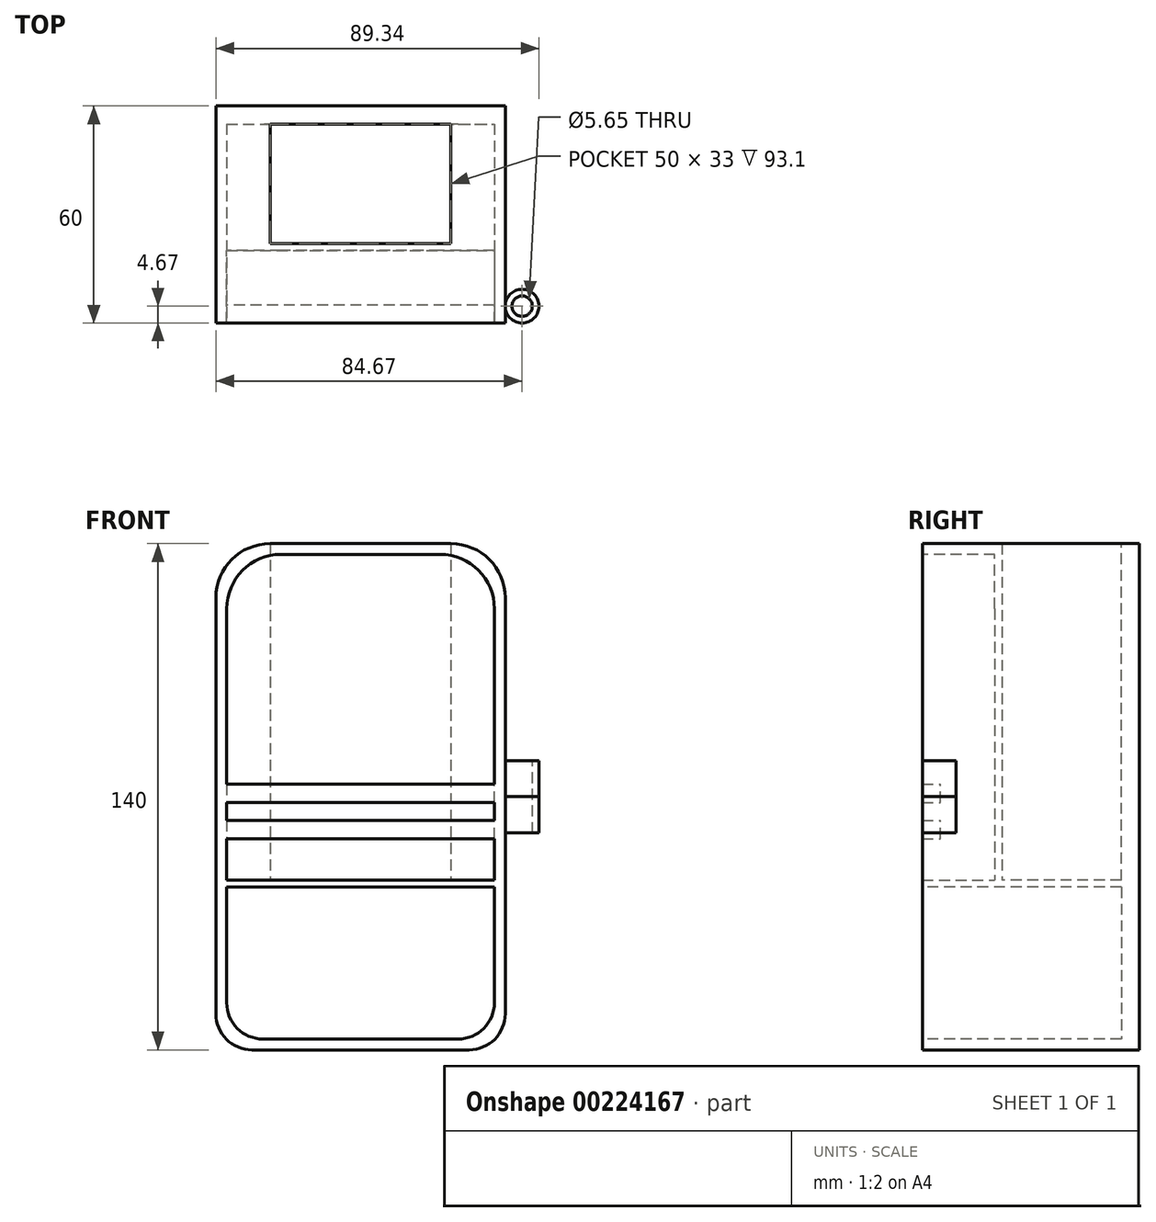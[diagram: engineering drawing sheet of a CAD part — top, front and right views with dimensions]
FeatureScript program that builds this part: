
annotation { "Feature Type Name" : "Feature", "Feature Type Description" : "" }
export const myFeature = defineFeature(function(context is Context, id is Id, definition is map)
    precondition{}
    {
        {
            var Q0;
            Q0=qCreatedBy(makeId("Front.planeOp"),FACE);
            var sketch = newSketch(context, id + "F0", { "sketchPlane" : qUnion([Q0])});
            skLineSegment(sketch, "E0.bottom", {"start": v(40, 70) * mm, "end": v(-40, 70) * mm});
            skLineSegment(sketch, "E0.top", {"start": v(40, -70) * mm, "end": v(-40, -70) * mm});
            skLineSegment(sketch, "E0.left", {"start": v(40, 70) * mm, "end": v(40, -70) * mm});
            skLineSegment(sketch, "E0.right", {"start": v(-40, 70) * mm, "end": v(-40, -70) * mm});
            skPoint(sketch, "E0.middle", {"position": v(0, 0) * mm});
            skSolve(sketch);
        }
        {
            var Q0;
            Q0=makeQuery(id+"F0.imprint","IMPRINT",FACE,{"disambiguationData":[TD([[makeQuery(id+"F0.imprint","IMPRINT",EDGE,{"derivedFrom":sQuery(id+"F0.wireOp",EDGE,"E0.bottom")}),1.0]])]});
            extrude(context, id + "F1", {"entities" : qUnion([Q0]), "oppositeDirection" : true, "depth" : 60 * mm});
        }
        {
            var Q0;
            Q0=makeQuery(id+"F1.opExtrude","SWEPT_EDGE",EDGE,{"disambiguationData":[OSD([sQuery(id+"F0.wireOp",EDGE,"E0.bottom"),sQuery(id+"F0.wireOp",EDGE,"E0.right")])]});
            fillet(context, id + "F2", {"entities" : qUnion([Q0]), "radius" : 15 * mm, "tangentPropagation" : true, "allowEdgeOverflow" : false});
        }
        {
            var Q0;
            Q0=makeQuery(id+"F1.opExtrude","SWEPT_EDGE",EDGE,{"disambiguationData":[OSD([sQuery(id+"F0.wireOp",EDGE,"E0.bottom"),sQuery(id+"F0.wireOp",EDGE,"E0.left")])]});
            fillet(context, id + "F3", {"entities" : qUnion([Q0]), "radius" : 15 * mm, "tangentPropagation" : true, "allowEdgeOverflow" : false});
        }
        {
            var Q0;
            Q0=makeQuery(id+"F1.opExtrude","SWEPT_EDGE",EDGE,{"disambiguationData":[OSD([sQuery(id+"F0.wireOp",EDGE,"E0.top"),sQuery(id+"F0.wireOp",EDGE,"E0.right")])]});
            var Q1;
            Q1=makeQuery(id+"F1.opExtrude","SWEPT_EDGE",EDGE,{"disambiguationData":[OSD([sQuery(id+"F0.wireOp",EDGE,"E0.top"),sQuery(id+"F0.wireOp",EDGE,"E0.left")])]});
            fillet(context, id + "F4", {"entities" : qUnion([Q0, Q1]), "radius" : 10 * mm, "tangentPropagation" : true, "allowEdgeOverflow" : false});
        }
        {
            var Q0;
            Q0=makeQuery(id+"F1.opExtrude","CAP_FACE",FACE,{"disambiguationData":[OSD([sQuery(id+"F0.wireOp",EDGE,"E0.bottom"),sQuery(id+"F0.wireOp",EDGE,"E0.top"),sQuery(id+"F0.wireOp",EDGE,"E0.left"),sQuery(id+"F0.wireOp",EDGE,"E0.right")])],"isStart":true});
            var sketch = newSketch(context, id + "F5", { "sketchPlane" : qUnion([Q0])});
            skLineSegment(sketch, "E1.bottom", {"start": v(22, 67) * mm, "end": v(-22, 67) * mm});
            skLineSegment(sketch, "E1.top", {"start": v(27, -67) * mm, "end": v(-27, -67) * mm});
            skLineSegment(sketch, "E1.left", {"start": v(37, 52) * mm, "end": v(37, -57) * mm});
            skLineSegment(sketch, "E1.right", {"start": v(-37, 52) * mm, "end": v(-37, -57) * mm});
            skPoint(sketch, "E1.middle", {"position": v(0, 0) * mm});
            skPoint(sketch, "E2.visualSharp", {"position": v(-37, 67) * mm});
            skArc(sketch, "E2.filletArc", {"start": v(-22, 67) * mm, "mid": v(-32.6, 62.6) * mm, "end": v(-37, 52) * mm});
            skPoint(sketch, "E3.visualSharp", {"position": v(37, 67) * mm});
            skArc(sketch, "E3.filletArc", {"start": v(37, 52) * mm, "mid": v(32.6, 62.6) * mm, "end": v(22, 67) * mm});
            skPoint(sketch, "E4.visualSharp", {"position": v(-37, -67) * mm});
            skArc(sketch, "E4.filletArc", {"start": v(-37, -57) * mm, "mid": v(-34.07, -64.07) * mm, "end": v(-27, -67) * mm});
            skPoint(sketch, "E5.visualSharp", {"position": v(37, -67) * mm});
            skArc(sketch, "E5.filletArc", {"start": v(27, -67) * mm, "mid": v(34.07, -64.07) * mm, "end": v(37, -57) * mm});
            skLineSegment(sketch, "E6", {"start": v(-37, -25) * mm, "end": v(37, -25) * mm});
            skSolve(sketch);
        }
        {
            var Q0;
            Q0=makeQuery(id+"F5.imprint","IMPRINT",FACE,{"disambiguationData":[TD([[makeQuery(id+"F5.imprint","IMPRINT",EDGE,{"derivedFrom":sQuery(id+"F5.wireOp",EDGE,"E1.top")}),-1.0]])]});
            extrude(context, id + "F6", {"entities" : qUnion([Q0]), "operationType" : NewBodyOperationType.REMOVE, "oppositeDirection" : true, "depth" : 55 * mm});
        }
        {
            var Q0;
            Q0=makeQuery(id+"F1.opExtrude","CAP_FACE",FACE,{"disambiguationData":[OSD([sQuery(id+"F0.wireOp",EDGE,"E0.bottom"),sQuery(id+"F0.wireOp",EDGE,"E0.top"),sQuery(id+"F0.wireOp",EDGE,"E0.left"),sQuery(id+"F0.wireOp",EDGE,"E0.right")])],"isStart":true});
            var sketch = newSketch(context, id + "F7", { "sketchPlane" : qUnion([Q0])});
            skLineSegment(sketch, "E7.bottom", {"start": v(22, 67) * mm, "end": v(-22, 67) * mm});
            skLineSegment(sketch, "E7.top", {"start": v(37, -25) * mm, "end": v(-37, -25) * mm});
            skLineSegment(sketch, "E7.left", {"start": v(37, 52) * mm, "end": v(37, -25) * mm});
            skLineSegment(sketch, "E7.right", {"start": v(-37, 52) * mm, "end": v(-37, -25) * mm});
            skPoint(sketch, "E7.middle", {"position": v(0, 21) * mm});
            skPoint(sketch, "E8.visualSharp", {"position": v(-37, 67) * mm});
            skArc(sketch, "E8.filletArc", {"start": v(-22, 67) * mm, "mid": v(-32.6, 62.6) * mm, "end": v(-37, 52) * mm});
            skPoint(sketch, "E9.visualSharp", {"position": v(37, 67) * mm});
            skArc(sketch, "E9.filletArc", {"start": v(37, 52) * mm, "mid": v(32.6, 62.6) * mm, "end": v(22, 67) * mm});
            skSolve(sketch);
        }
        {
            var Q0;
            Q0=makeQuery(id+"F7.imprint","IMPRINT",FACE,{"disambiguationData":[TD([[makeQuery(id+"F7.imprint","IMPRINT",EDGE,{"derivedFrom":sQuery(id+"F7.wireOp",EDGE,"E7.bottom")}),1.0]])]});
            extrude(context, id + "F8", {"entities" : qUnion([Q0]), "operationType" : NewBodyOperationType.REMOVE, "oppositeDirection" : true, "depth" : 20 * mm});
        }
        {
            var Q0;
            Q0=makeQuery(id+"F8.boolean.opBoolean","COPY",FACE,{"derivedFrom":makeQuery(id+"F8.opExtrude","CAP_FACE",FACE,{"disambiguationData":[OSD([sQuery(id+"F7.wireOp",EDGE,"E7.bottom"),sQuery(id+"F7.wireOp",EDGE,"E7.top"),sQuery(id+"F7.wireOp",EDGE,"E7.left"),sQuery(id+"F7.wireOp",EDGE,"E7.right"),sQuery(id+"F7.wireOp",EDGE,"E8.filletArc"),sQuery(id+"F7.wireOp",EDGE,"E9.filletArc")])],"isStart":false})});
            var sketch = newSketch(context, id + "F9", { "sketchPlane" : qUnion([Q0])});
            skLineSegment(sketch, "E10.bottom", {"start": v(-37, -25) * mm, "end": v(37, -25) * mm});
            skLineSegment(sketch, "E10.top", {"start": v(-37, -23) * mm, "end": v(37, -23) * mm});
            skLineSegment(sketch, "E10.left", {"start": v(-37, -25) * mm, "end": v(-37, -23) * mm});
            skLineSegment(sketch, "E10.right", {"start": v(37, -25) * mm, "end": v(37, -23) * mm});
            skSolve(sketch);
        }
        {
            var Q0;
            Q0 = qSketchRegion(id + "F9", true);
            extrude(context, id + "F10", {"entities" : qUnion([Q0]), "operationType" : NewBodyOperationType.ADD, "depth" : 20 * mm});
        }
        {
            var Q0;
            Q0=makeQuery(id+"F1.opExtrude","SWEPT_FACE",FACE,{"disambiguationData":[OSD([sQuery(id+"F0.wireOp",EDGE,"E0.bottom")])]});
            var sketch = newSketch(context, id + "F11", { "sketchPlane" : qUnion([Q0])});
            skLineSegment(sketch, "E11.bottom", {"start": v(-25, 20) * mm, "end": v(25, 20) * mm});
            skLineSegment(sketch, "E11.top", {"start": v(-25, 55) * mm, "end": v(25, 55) * mm});
            skLineSegment(sketch, "E11.left", {"start": v(-25, 20) * mm, "end": v(-25, 55) * mm});
            skLineSegment(sketch, "E11.right", {"start": v(25, 20) * mm, "end": v(25, 55) * mm});
            skSolve(sketch);
        }
        {
            var Q0;
            Q0 = qSketchRegion(id + "F11", true);
            extrude(context, id + "F12", {"entities" : qUnion([Q0]), "operationType" : NewBodyOperationType.REMOVE, "oppositeDirection" : true, "depth" : 93.1 * mm});
        }
        {
            var Q0;
            Q0=makeQuery(id+"F12.boolean.opBoolean","COPY",FACE,{"derivedFrom":makeQuery(id+"F12.opExtrude","SWEPT_FACE",FACE,{"disambiguationData":[OSD([sQuery(id+"F11.wireOp",EDGE,"E11.left")])]})});
            var sketch = newSketch(context, id + "F13", { "sketchPlane" : qUnion([Q0])});
            skLineSegment(sketch, "E12.bottom", {"start": v(20, 70) * mm, "end": v(22, 70) * mm});
            skLineSegment(sketch, "E12.top", {"start": v(20, -23.1) * mm, "end": v(22, -23.1) * mm});
            skLineSegment(sketch, "E12.left", {"start": v(20, 70) * mm, "end": v(20, -23.1) * mm});
            skLineSegment(sketch, "E12.right", {"start": v(22, 70) * mm, "end": v(22, -23.1) * mm});
            skSolve(sketch);
        }
        {
            var Q0;
            Q0 = qSketchRegion(id + "F13", true);
            extrude(context, id + "F14", {"entities" : qUnion([Q0]), "operationType" : NewBodyOperationType.ADD, "depth" : 50 * mm});
        }
        {
            var Q0;
            {var subQ1=sQuery(id+"F7.wireOp",EDGE,"E8.filletArc");var subQ2=sQuery(id+"F7.wireOp",EDGE,"E7.right");Q0=makeQuery(id+"F10.boolean.opBoolean","SPLIT",FACE,{"disambiguationData":[TD([makeQuery(id+"F8.boolean.opBoolean","COPY",FACE,{"derivedFrom":makeQuery(id+"F8.opExtrude","SWEPT_FACE",FACE,{"disambiguationData":[OSD([subQ1])]})})])],"derivedFrom":makeQuery(id+"F8.boolean.opBoolean","MERGE",FACE,{"derivedFrom":[makeQuery(id+"F6.boolean.opBoolean","COPY",FACE,{"derivedFrom":makeQuery(id+"F6.opExtrude","SWEPT_FACE",FACE,{"disambiguationData":[OSD([sQuery(id+"F5.wireOp",EDGE,"E1.right")])]})}),makeQuery(id+"F8.opExtrude","SWEPT_FACE",FACE,{"disambiguationData":[OSD([subQ2])]})]})});}
            var sketch = newSketch(context, id + "F15", { "sketchPlane" : qUnion([Q0])});
            skLineSegment(sketch, "E13.bottom", {"start": v(0, -1.57) * mm, "end": v(5, -1.57) * mm});
            skLineSegment(sketch, "E13.top", {"start": v(0, 3.43) * mm, "end": v(5, 3.43) * mm});
            skLineSegment(sketch, "E13.left", {"start": v(0, -1.57) * mm, "end": v(0, 3.43) * mm});
            skLineSegment(sketch, "E13.right", {"start": v(5, -1.57) * mm, "end": v(5, 3.43) * mm});
            skLineSegment(sketch, "E14.bottom", {"start": v(0, -11.57) * mm, "end": v(5, -11.57) * mm});
            skLineSegment(sketch, "E14.top", {"start": v(0, -6.57) * mm, "end": v(5, -6.57) * mm});
            skLineSegment(sketch, "E14.left", {"start": v(0, -11.57) * mm, "end": v(0, -6.57) * mm});
            skLineSegment(sketch, "E14.right", {"start": v(5, -11.57) * mm, "end": v(5, -6.57) * mm});
            skSolve(sketch);
        }
        {
            var Q0;
            Q0 = qSketchRegion(id + "F15", true);
            extrude(context, id + "F16", {"entities" : qUnion([Q0]), "operationType" : NewBodyOperationType.ADD, "depth" : 74 * mm});
        }
        {
            var Q0;
            Q0=qCreatedBy(makeId("Top.planeOp"),FACE);
            var sketch = newSketch(context, id + "F17", { "sketchPlane" : qUnion([Q0])});
            skCircle(sketch, "E15", {"center": v(44.67, 4.67) * mm, "radius": 4.67 * mm});
            skSolve(sketch);
        }
        {
            var Q0;
            Q0 = qSketchRegion(id + "F17", true);
            extrude(context, id + "F18", {"entities" : qUnion([Q0]), "operationType" : NewBodyOperationType.ADD, "depth" : 10 * mm});
        }
        {
            var Q0;
            Q0=makeQuery(id+"F18.opExtrude","CAP_FACE",FACE,{"disambiguationData":[OSD([sQuery(id+"F17.wireOp",EDGE,"E15")])],"isStart":true});
            var sketch = newSketch(context, id + "F19", { "sketchPlane" : qUnion([Q0])});
            skCircle(sketch, "E16", {"center": v(44.67, -4.67) * mm, "radius": 4.61 * mm});
            skSolve(sketch);
        }
        {
            var Q0;
            Q0 = qSketchRegion(id + "F19", true);
            extrude(context, id + "F20", {"entities" : qUnion([Q0]), "operationType" : NewBodyOperationType.ADD, "depth" : 10 * mm});
        }
        {
            var Q0;
            Q0=makeQuery(id+"F18.opExtrude","CAP_FACE",FACE,{"disambiguationData":[OSD([sQuery(id+"F17.wireOp",EDGE,"E15")])],"isStart":false});
            var sketch = newSketch(context, id + "F21", { "sketchPlane" : qUnion([Q0])});
            skCircle(sketch, "E17", {"center": v(44.67, 4.67) * mm, "radius": 2.82 * mm});
            skSolve(sketch);
        }
        {
            var Q0;
            Q0 = qSketchRegion(id + "F21", true);
            extrude(context, id + "F22", {"entities" : qUnion([Q0]), "operationType" : NewBodyOperationType.REMOVE, "oppositeDirection" : true, "depth" : 30.5 * mm});
        }
    });
